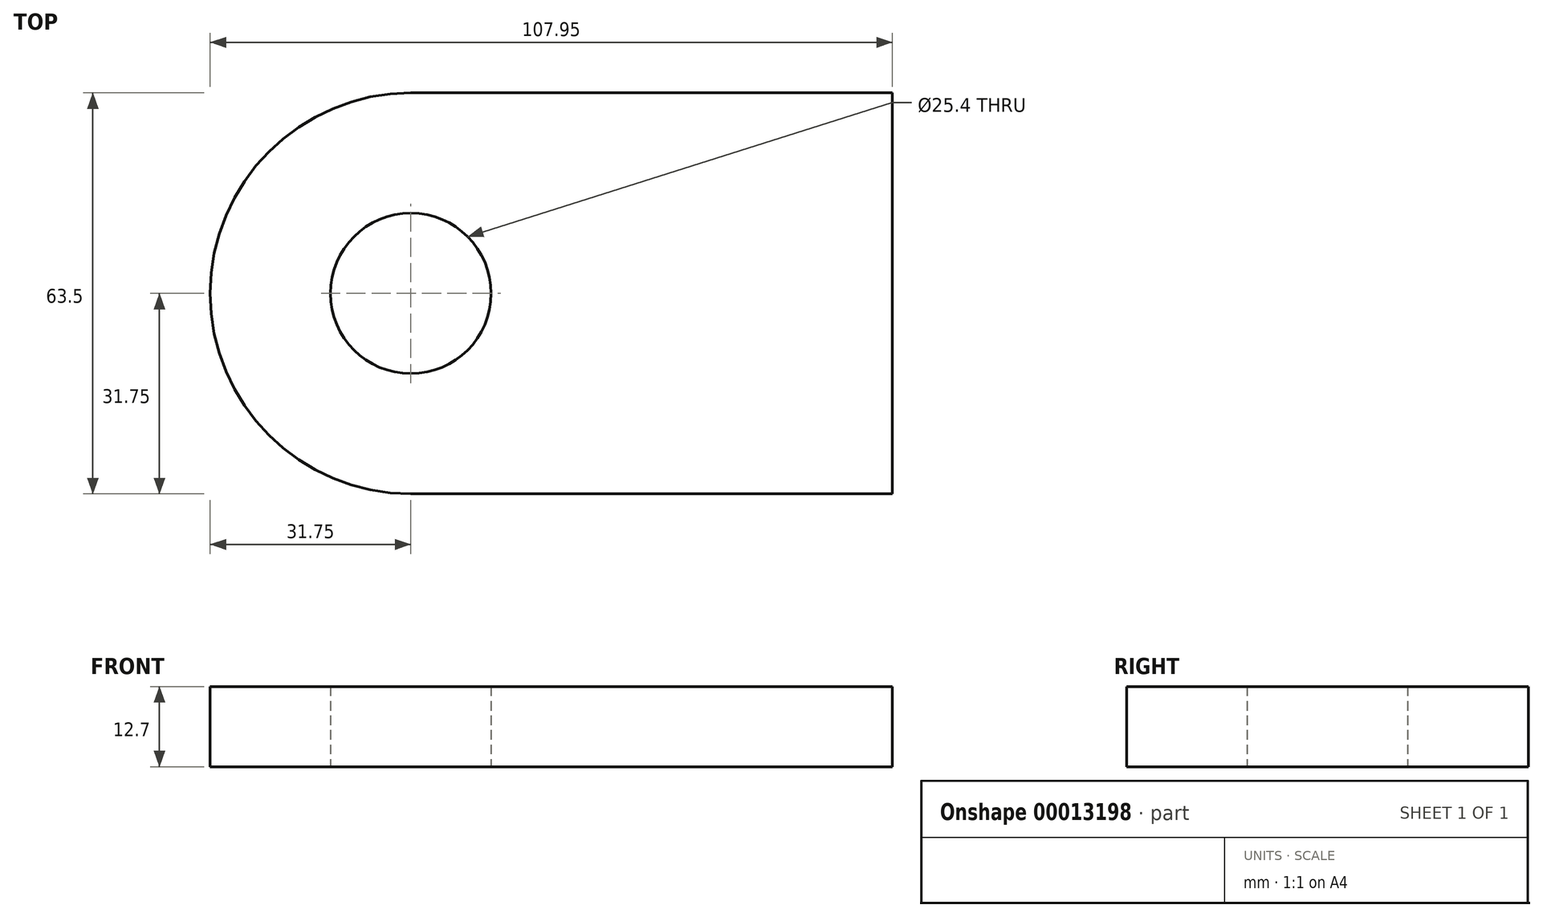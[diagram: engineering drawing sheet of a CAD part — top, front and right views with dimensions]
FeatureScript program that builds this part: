
annotation { "Feature Type Name" : "Feature", "Feature Type Description" : "" }
export const myFeature = defineFeature(function(context is Context, id is Id, definition is map)
    precondition{}
    {
        {
            var Q0;
            Q0=qCreatedBy(makeId("Top.planeOp"),FACE);
            var sketch = newSketch(context, id + "F0", { "sketchPlane" : qUnion([Q0])});
            skLineSegment(sketch, "E0.rect.bottom", {"start": v(-38.1, -31.75) * mm, "end": v(38.1, -31.75) * mm});
            skLineSegment(sketch, "E0.rect.top", {"start": v(-38.1, 31.75) * mm, "end": v(38.1, 31.75) * mm});
            skLineSegment(sketch, "E0.rect.left", {"start": v(-38.1, -31.75) * mm, "end": v(-38.1, 31.75) * mm});
            skLineSegment(sketch, "E0.rect.right", {"start": v(38.1, -31.75) * mm, "end": v(38.1, 31.75) * mm});
            skPoint(sketch, "E0.rect.middle", {"position": v(0, 0) * mm});
            skCircle(sketch, "E1", {"center": v(-38.1, 0) * mm, "radius": 31.75 * mm});
            skCircle(sketch, "E2", {"center": v(-38.1, 0) * mm, "radius": 12.7 * mm});
            skSolve(sketch);
        }
        {
            var Q0;
            Q0 = qSketchRegion(id + "F0", true);
            extrude(context, id + "F1", {"entities" : qUnion([Q0]), "depth" : 12.7 * mm});
        }
    });
